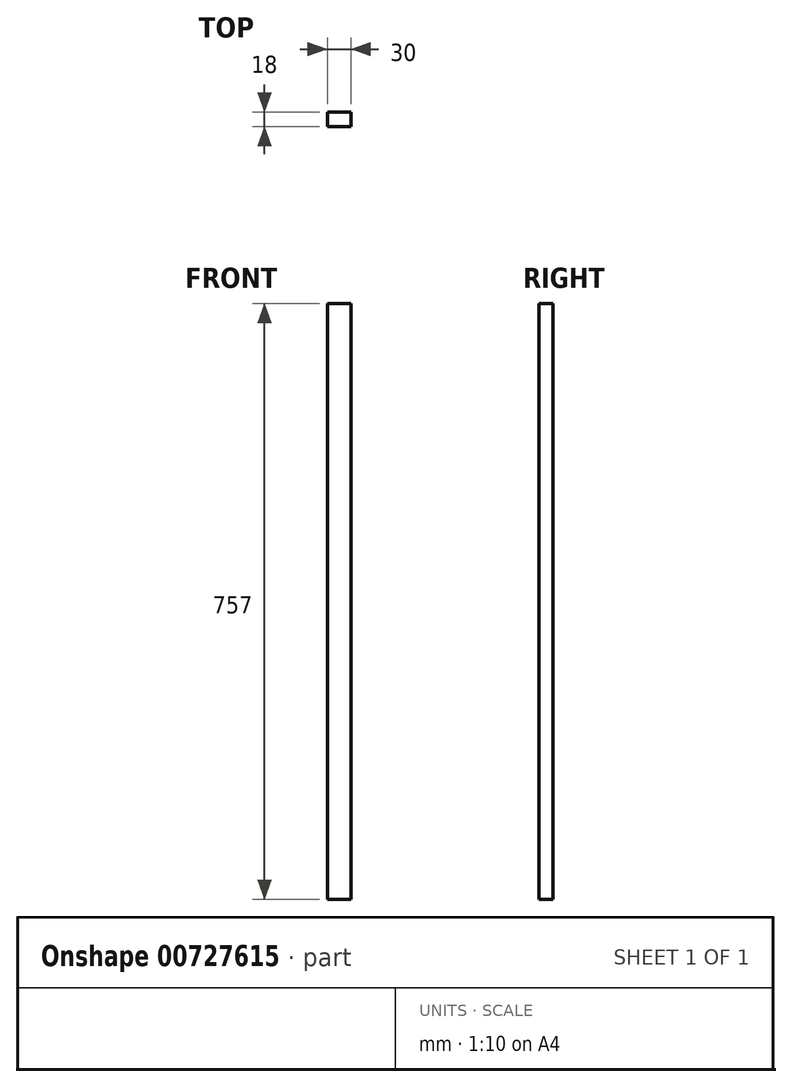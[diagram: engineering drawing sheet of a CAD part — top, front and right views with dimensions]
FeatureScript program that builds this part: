
annotation { "Feature Type Name" : "Feature", "Feature Type Description" : "" }
export const myFeature = defineFeature(function(context is Context, id is Id, definition is map)
    precondition{}
    {
        {
            var Q0;
            Q0=qCreatedBy(makeId("Front.planeOp"),FACE);
            var sketch = newSketch(context, id + "F0", { "sketchPlane" : qUnion([Q0])});
            skLineSegment(sketch, "E0.bottom", {"start": v(-15, -378.5) * mm, "end": v(15, -378.5) * mm});
            skLineSegment(sketch, "E0.top", {"start": v(-15, 378.5) * mm, "end": v(15, 378.5) * mm});
            skLineSegment(sketch, "E0.left", {"start": v(-15, -378.5) * mm, "end": v(-15, 378.5) * mm});
            skLineSegment(sketch, "E0.right", {"start": v(15, -378.5) * mm, "end": v(15, 378.5) * mm});
            skPoint(sketch, "E0.middle", {"position": v(0, 0) * mm});
            skSolve(sketch);
        }
        {
            var Q0;
            Q0 = qSketchRegion(id + "F0", true);
            extrude(context, id + "F1", {"entities" : qUnion([Q0]), "depth" : 18 * mm, "offsetDistance" : 25 * mm});
        }
    });
